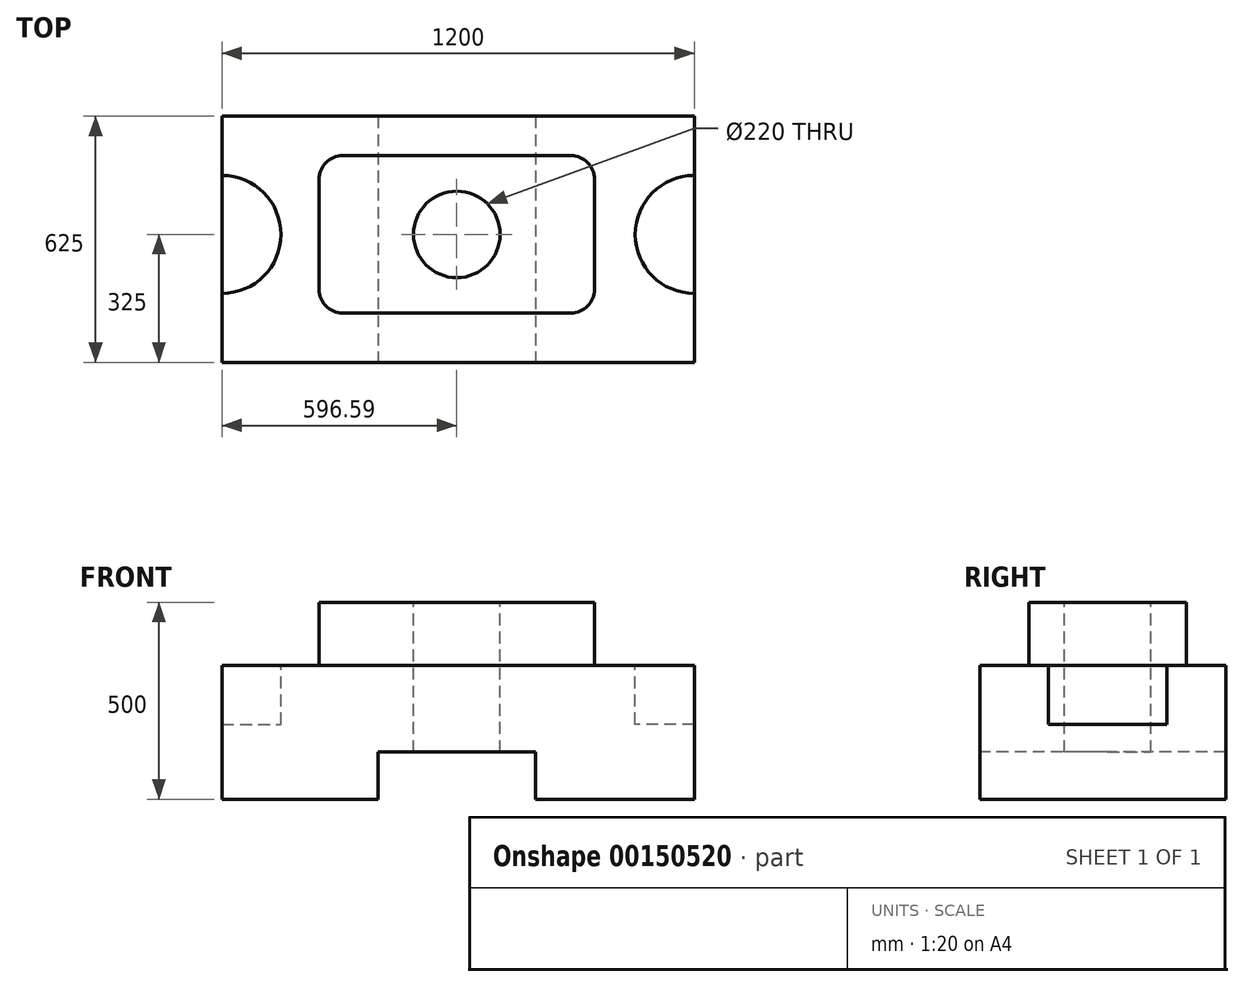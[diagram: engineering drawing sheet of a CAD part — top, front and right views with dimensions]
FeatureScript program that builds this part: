
annotation { "Feature Type Name" : "Feature", "Feature Type Description" : "" }
export const myFeature = defineFeature(function(context is Context, id is Id, definition is map)
    precondition{}
    {
        {
            var Q0;
            Q0=qCreatedBy(makeId("Top.planeOp"),FACE);
            var sketch = newSketch(context, id + "F0", { "sketchPlane" : qUnion([Q0])});
            skLineSegment(sketch, "E0.bottom", {"start": v(-596.59, -300) * mm, "end": v(603.41, -300) * mm});
            skLineSegment(sketch, "E0.top", {"start": v(-596.59, 300) * mm, "end": v(603.41, 300) * mm});
            skLineSegment(sketch, "E0.left", {"start": v(-596.59, -300) * mm, "end": v(-596.59, 300) * mm});
            skLineSegment(sketch, "E0.right", {"start": v(603.41, -300) * mm, "end": v(603.41, 300) * mm});
            skPoint(sketch, "E0.middle", {"position": v(3.41, 0) * mm});
            skSolve(sketch);
        }
        {
            var Q0;
            Q0=makeQuery(id+"F0.imprint","IMPRINT",FACE,{"disambiguationData":[TD([[makeQuery(id+"F0.imprint","IMPRINT",EDGE,{"derivedFrom":sQuery(id+"F0.wireOp",EDGE,"E0.bottom")}),1.0]])]});
            extrude(context, id + "F1", {"entities" : qUnion([Q0]), "depth" : 340 * mm});
        }
        {
            var Q0;
            Q0=makeQuery(id+"F1.opExtrude","CAP_FACE",FACE,{"disambiguationData":[OSD([sQuery(id+"F0.wireOp",EDGE,"E0.bottom"),sQuery(id+"F0.wireOp",EDGE,"E0.top"),sQuery(id+"F0.wireOp",EDGE,"E0.left"),sQuery(id+"F0.wireOp",EDGE,"E0.right")])],"isStart":false});
            var sketch = newSketch(context, id + "F2", { "sketchPlane" : qUnion([Q0])});
            skCircle(sketch, "E1", {"center": v(-596.59, 0) * mm, "radius": 150 * mm});
            skSolve(sketch);
        }
        {
            var Q0;
            {var subQ0=sQuery(id+"F2.wireOp",EDGE,"E1");var subQ1=makeQuery(id+"F1.opExtrude","CAP_EDGE",EDGE,{"disambiguationData":[OSD([sQuery(id+"F0.wireOp",EDGE,"E0.left")])],"isStart":false});var subQ2=makeQuery(id+"F2.imprint","INTERSECT",VERTEX,{"disambiguationData":[OD(0.0)],"derivedFrom":[subQ1,subQ0]});Q0=makeQuery(id+"F2.imprint","IMPRINT",FACE,{"disambiguationData":[TD([[makeQuery(id+"F2.imprint","IMPRINT",EDGE,{"disambiguationData":[TD([[subQ2,-1.0]])],"derivedFrom":subQ0}),1.0]])]});}
            extrude(context, id + "F3", {"entities" : qUnion([Q0]), "operationType" : NewBodyOperationType.REMOVE, "oppositeDirection" : true, "depth" : 150 * mm});
        }
        {
            var Q0;
            Q0=makeQuery(id+"F1.opExtrude","CAP_FACE",FACE,{"disambiguationData":[OSD([sQuery(id+"F0.wireOp",EDGE,"E0.bottom"),sQuery(id+"F0.wireOp",EDGE,"E0.top"),sQuery(id+"F0.wireOp",EDGE,"E0.left"),sQuery(id+"F0.wireOp",EDGE,"E0.right")])],"isStart":false});
            var sketch = newSketch(context, id + "F4", { "sketchPlane" : qUnion([Q0])});
            skCircle(sketch, "E2", {"center": v(603.41, 0) * mm, "radius": 150 * mm});
            skSolve(sketch);
        }
        {
            var Q0;
            {var subQ0=sQuery(id+"F4.wireOp",EDGE,"E2");var subQ1=makeQuery(id+"F1.opExtrude","CAP_EDGE",EDGE,{"disambiguationData":[OSD([sQuery(id+"F0.wireOp",EDGE,"E0.right")])],"isStart":false});var subQ2=makeQuery(id+"F4.imprint","INTERSECT",VERTEX,{"disambiguationData":[OD(0.0)],"derivedFrom":[subQ1,subQ0]});Q0=makeQuery(id+"F4.imprint","IMPRINT",FACE,{"disambiguationData":[TD([[makeQuery(id+"F4.imprint","IMPRINT",EDGE,{"disambiguationData":[TD([[subQ2,1.0]])],"derivedFrom":subQ0}),1.0]])]});}
            extrude(context, id + "F5", {"entities" : qUnion([Q0]), "operationType" : NewBodyOperationType.REMOVE, "oppositeDirection" : true, "depth" : 150 * mm});
        }
        {
            var Q0;
            Q0=makeQuery(id+"F1.opExtrude","CAP_FACE",FACE,{"disambiguationData":[OSD([sQuery(id+"F0.wireOp",EDGE,"E0.bottom"),sQuery(id+"F0.wireOp",EDGE,"E0.top"),sQuery(id+"F0.wireOp",EDGE,"E0.left"),sQuery(id+"F0.wireOp",EDGE,"E0.right")])],"isStart":false});
            var sketch = newSketch(context, id + "F6", { "sketchPlane" : qUnion([Q0])});
            skLineSegment(sketch, "E3.bottom", {"start": v(-350, -200) * mm, "end": v(350, -200) * mm});
            skLineSegment(sketch, "E3.top", {"start": v(-350, 200) * mm, "end": v(350, 200) * mm});
            skLineSegment(sketch, "E3.left", {"start": v(-350, -200) * mm, "end": v(-350, 200) * mm});
            skLineSegment(sketch, "E3.right", {"start": v(350, -200) * mm, "end": v(350, 200) * mm});
            skPoint(sketch, "E3.middle", {"position": v(0, 0) * mm});
            skSolve(sketch);
        }
        {
            var Q0;
            Q0=makeQuery(id+"F6.imprint","IMPRINT",FACE,{"disambiguationData":[TD([[makeQuery(id+"F6.imprint","IMPRINT",EDGE,{"derivedFrom":sQuery(id+"F6.wireOp",EDGE,"E3.bottom")}),1.0]])]});
            extrude(context, id + "F7", {"entities" : qUnion([Q0]), "operationType" : NewBodyOperationType.ADD, "depth" : 160 * mm});
        }
        {
            var Q0;
            Q0=makeQuery(id+"F7.opExtrude","CAP_FACE",FACE,{"disambiguationData":[OSD([sQuery(id+"F6.wireOp",EDGE,"E3.bottom"),sQuery(id+"F6.wireOp",EDGE,"E3.top"),sQuery(id+"F6.wireOp",EDGE,"E3.left"),sQuery(id+"F6.wireOp",EDGE,"E3.right")])],"isStart":false});
            var sketch = newSketch(context, id + "F8", { "sketchPlane" : qUnion([Q0])});
            skCircle(sketch, "E4", {"center": v(0, 0) * mm, "radius": 110 * mm});
            skSolve(sketch);
        }
        {
            var Q0;
            Q0=makeQuery(id+"F8.imprint","IMPRINT",FACE,{"disambiguationData":[TD([[makeQuery(id+"F8.imprint","IMPRINT",EDGE,{"derivedFrom":sQuery(id+"F8.wireOp",EDGE,"E4")}),1.0]])]});
            extrude(context, id + "F9", {"entities" : qUnion([Q0]), "operationType" : NewBodyOperationType.REMOVE, "endBound" : BoundingType.THROUGH_ALL, "oppositeDirection" : true, "depth" : 25 * mm});
        }
        {
            var Q0;
            Q0=makeQuery(id+"F1.opExtrude","SWEPT_FACE",FACE,{"disambiguationData":[OSD([sQuery(id+"F0.wireOp",EDGE,"E0.bottom")])]});
            extrude(context, id + "F10", {"entities" : qUnion([Q0]), "operationType" : NewBodyOperationType.ADD, "depth" : 25 * mm});
        }
        {
            var Q0;
            Q0=makeQuery(id+"F10.opExtrude","CAP_FACE",FACE,{"disambiguationData":[OSD([sQuery(id+"F0.wireOp",EDGE,"E0.bottom")])],"isStart":false});
            var sketch = newSketch(context, id + "F11", { "sketchPlane" : qUnion([Q0])});
            skLineSegment(sketch, "E5.bottom", {"start": v(-200, -120) * mm, "end": v(200, -120) * mm});
            skLineSegment(sketch, "E5.top", {"start": v(-200, 120) * mm, "end": v(200, 120) * mm});
            skLineSegment(sketch, "E5.left", {"start": v(-200, -120) * mm, "end": v(-200, 120) * mm});
            skLineSegment(sketch, "E5.right", {"start": v(200, -120) * mm, "end": v(200, 120) * mm});
            skPoint(sketch, "E5.middle", {"position": v(0, 0) * mm});
            skSolve(sketch);
        }
        {
            var Q0;
            {var subQ0=sQuery(id+"F11.wireOp",EDGE,"E5.top");Q0=makeQuery(id+"F11.imprint","IMPRINT",FACE,{"disambiguationData":[TD([[makeQuery(id+"F11.imprint","IMPRINT",EDGE,{"derivedFrom":subQ0}),-1.0]])]});}
            extrude(context, id + "F12", {"entities" : qUnion([Q0]), "operationType" : NewBodyOperationType.REMOVE, "endBound" : BoundingType.THROUGH_ALL, "oppositeDirection" : true, "depth" : 25 * mm});
        }
        {
            var Q0;
            Q0=makeQuery(id+"F7.opExtrude","SWEPT_EDGE",EDGE,{"disambiguationData":[OSD([sQuery(id+"F6.wireOp",EDGE,"E3.bottom"),sQuery(id+"F6.wireOp",EDGE,"E3.left")])]});
            var Q1;
            Q1=makeQuery(id+"F7.opExtrude","SWEPT_EDGE",EDGE,{"disambiguationData":[OSD([sQuery(id+"F6.wireOp",EDGE,"E3.bottom"),sQuery(id+"F6.wireOp",EDGE,"E3.right")])]});
            var Q2;
            Q2=makeQuery(id+"F7.opExtrude","SWEPT_EDGE",EDGE,{"disambiguationData":[OSD([sQuery(id+"F6.wireOp",EDGE,"E3.top"),sQuery(id+"F6.wireOp",EDGE,"E3.right")])]});
            var Q3;
            Q3=makeQuery(id+"F7.opExtrude","SWEPT_EDGE",EDGE,{"disambiguationData":[OSD([sQuery(id+"F6.wireOp",EDGE,"E3.top"),sQuery(id+"F6.wireOp",EDGE,"E3.left")])]});
            fillet(context, id + "F13", {"entities" : qUnion([Q0, Q1, Q2, Q3]), "radius" : 60 * mm, "tangentPropagation" : true, "allowEdgeOverflow" : false});
        }
    });
